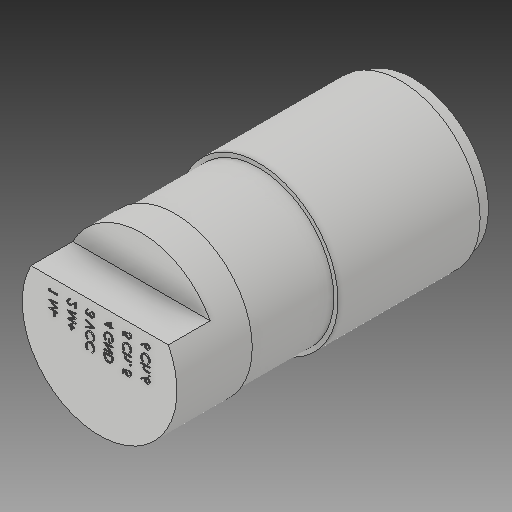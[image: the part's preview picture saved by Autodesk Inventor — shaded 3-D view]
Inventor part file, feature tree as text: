
AUTODESK INVENTOR PART (.ipt)
format: ipt  version: 2017 (Build 210142000, 142)  size: 846,848 bytes
history: native  units: in
note: dims shown in document units (in); Inventor stores cm internally (conversion verified against a paired STEP export)
features: other x3, sketch x1
ambient origin geometry x8: Origin, YZ Plane, XZ Plane, XY Plane, X Axis, Y Axis, Z Axis, Center Point
bodies: Solid1 (feature_tree)
feature tree (4):
  other  "am-2964NeveRest-noGearbox.ipt"
  other  "Solid1::am-2964NeveRest-noGearbox.ipt"
  other  "TaggingFeature1"
  sketch  "Sketch1"  dims[d0=0.3937in]
